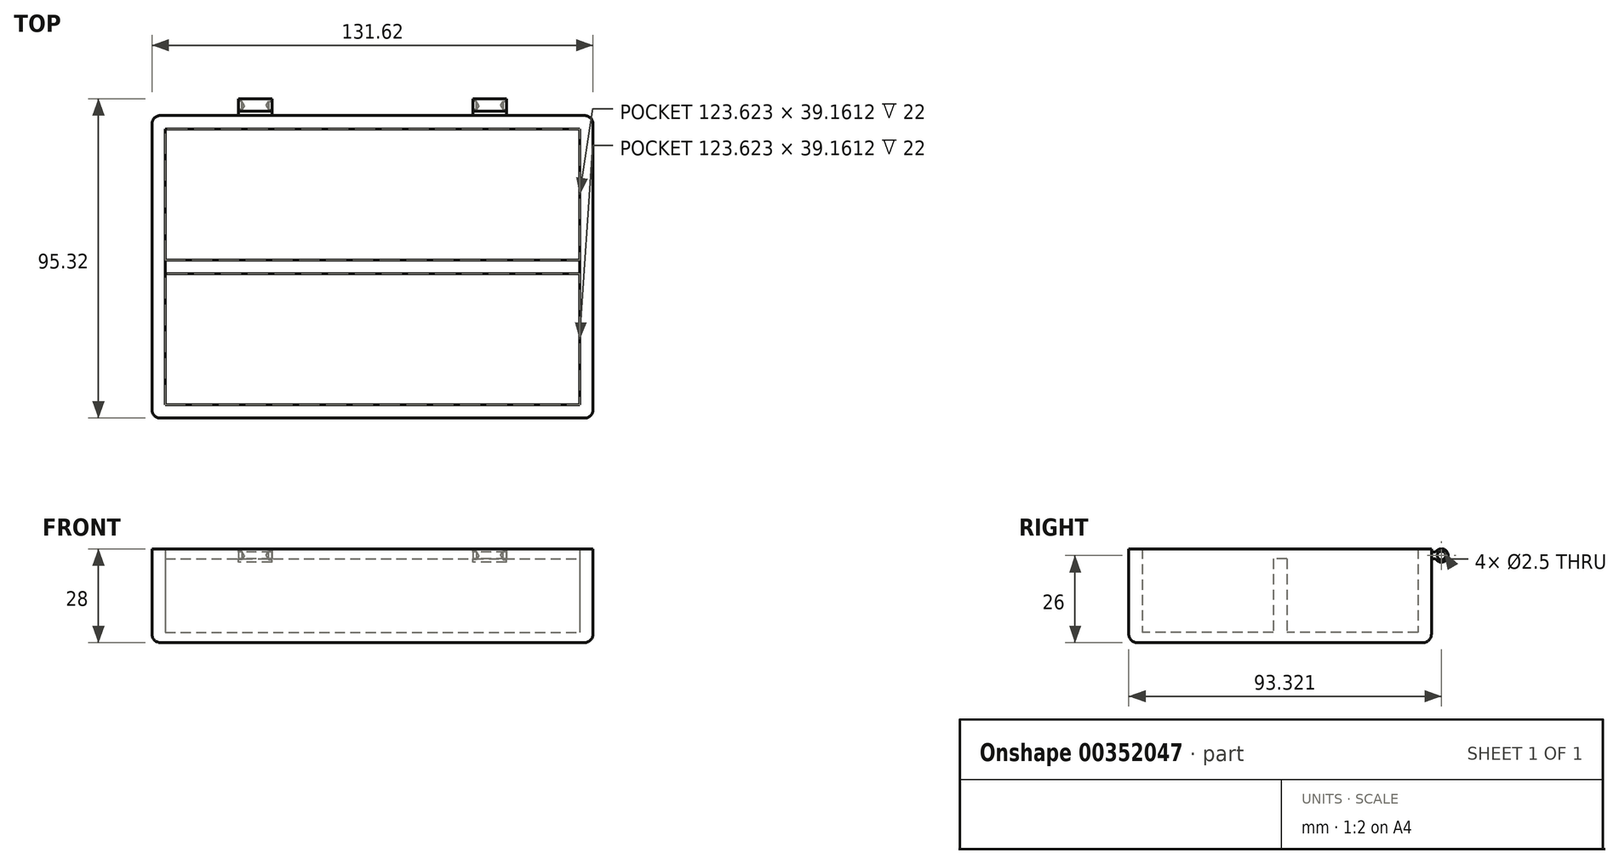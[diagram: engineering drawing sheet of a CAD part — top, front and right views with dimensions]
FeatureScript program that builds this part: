
annotation { "Feature Type Name" : "Feature", "Feature Type Description" : "" }
export const myFeature = defineFeature(function(context is Context, id is Id, definition is map)
    precondition{}
    {
        {
            var Q0;
            Q0=qCreatedBy(makeId("Top.planeOp"),FACE);
            var sketch = newSketch(context, id + "F0", { "sketchPlane" : qUnion([Q0])});
            skLineSegment(sketch, "E0.bottom", {"start": v(-65.81, 45.16) * mm, "end": v(65.81, 45.16) * mm});
            skLineSegment(sketch, "E0.top", {"start": v(-65.81, -45.16) * mm, "end": v(65.81, -45.16) * mm});
            skLineSegment(sketch, "E0.left", {"start": v(-65.81, 45.16) * mm, "end": v(-65.81, -45.16) * mm});
            skLineSegment(sketch, "E0.right", {"start": v(65.81, 45.16) * mm, "end": v(65.81, -45.16) * mm});
            skPoint(sketch, "E0.middle", {"position": v(0, 0) * mm});
            skSolve(sketch);
        }
        {
            var Q0;
            Q0 = qSketchRegion(id + "F0", true);
            extrude(context, id + "F1", {"entities" : qUnion([Q0]), "depth" : 3 * mm});
        }
        {
            var Q0;
            Q0=makeQuery(id+"F1.opExtrude","CAP_FACE",FACE,{"disambiguationData":[OSD([sQuery(id+"F0.wireOp",EDGE,"E0.bottom"),sQuery(id+"F0.wireOp",EDGE,"E0.top"),sQuery(id+"F0.wireOp",EDGE,"E0.left"),sQuery(id+"F0.wireOp",EDGE,"E0.right")])],"isStart":false});
            var sketch = newSketch(context, id + "F2", { "sketchPlane" : qUnion([Q0])});
            skLineSegment(sketch, "E1.bottom", {"start": v(-61.81, 41.16) * mm, "end": v(61.81, 41.16) * mm});
            skLineSegment(sketch, "E1.top", {"start": v(-61.81, -41.16) * mm, "end": v(61.81, -41.16) * mm});
            skLineSegment(sketch, "E1.left", {"start": v(-61.81, 41.16) * mm, "end": v(-61.81, -41.16) * mm});
            skLineSegment(sketch, "E1.right", {"start": v(61.81, 41.16) * mm, "end": v(61.81, -41.16) * mm});
            skPoint(sketch, "E1.middle", {"position": v(0, 0) * mm});
            skSolve(sketch);
        }
        {
            var Q0;
            Q0=makeQuery(id+"F2.imprint","IMPRINT",FACE,{"disambiguationData":[TD([[makeQuery(id+"F2.imprint","IMPRINT",EDGE,{"derivedFrom":sQuery(id+"F2.wireOp",EDGE,"E1.bottom")}),1.0]])]});
            extrude(context, id + "F3", {"entities" : qUnion([Q0]), "operationType" : NewBodyOperationType.ADD, "depth" : 25 * mm});
        }
        {
            var Q0;
            Q0=makeQuery(id+"F1.opExtrude","CAP_FACE",FACE,{"disambiguationData":[OSD([sQuery(id+"F0.wireOp",EDGE,"E0.bottom"),sQuery(id+"F0.wireOp",EDGE,"E0.top"),sQuery(id+"F0.wireOp",EDGE,"E0.left"),sQuery(id+"F0.wireOp",EDGE,"E0.right")])],"isStart":false});
            var sketch = newSketch(context, id + "F4", { "sketchPlane" : qUnion([Q0])});
            skLineSegment(sketch, "E2.bottom", {"start": v(-61.81, 41.16) * mm, "end": v(61.81, 41.16) * mm});
            skLineSegment(sketch, "E2.top", {"start": v(-61.81, 2) * mm, "end": v(61.81, 2) * mm});
            skLineSegment(sketch, "E2.left", {"start": v(-61.81, 41.16) * mm, "end": v(-61.81, 2) * mm});
            skLineSegment(sketch, "E2.right", {"start": v(61.81, 41.16) * mm, "end": v(61.81, 2) * mm});
            skLineSegment(sketch, "E3.bottom", {"start": v(-61.81, -2) * mm, "end": v(61.81, -2) * mm});
            skLineSegment(sketch, "E3.top", {"start": v(-61.81, -41.16) * mm, "end": v(61.81, -41.16) * mm});
            skLineSegment(sketch, "E3.left", {"start": v(-61.81, -2) * mm, "end": v(-61.81, -41.16) * mm});
            skLineSegment(sketch, "E3.right", {"start": v(61.81, -2) * mm, "end": v(61.81, -41.16) * mm});
            skSolve(sketch);
        }
        {
            var Q0;
            {var subQ0=sQuery(id+"F4.wireOp",EDGE,"E2.top");Q0=makeQuery(id+"F4.imprint","IMPRINT",FACE,{"disambiguationData":[TD([[makeQuery(id+"F4.imprint","IMPRINT",EDGE,{"derivedFrom":subQ0}),-1.0]])]});}
            extrude(context, id + "F5", {"entities" : qUnion([Q0]), "operationType" : NewBodyOperationType.ADD, "depth" : 25 * mm});
        }
        {
            var Q0;
            {var subQ0=sQuery(id+"F0.wireOp",EDGE,"E0.right");var subQ1=sQuery(id+"F0.wireOp",EDGE,"E0.bottom");Q0=makeQuery(id+"F3.boolean.opBoolean","MERGE",EDGE,{"derivedFrom":[makeQuery(id+"F1.opExtrude","SWEPT_EDGE",EDGE,{"disambiguationData":[OSD([subQ1,subQ0])]}),makeQuery(id+"F3.opExtrude","SWEPT_EDGE",EDGE,{"disambiguationData":[OSD([subQ1,subQ0])]})]});}
            var Q1;
            {var subQ0=sQuery(id+"F0.wireOp",EDGE,"E0.right");var subQ1=sQuery(id+"F0.wireOp",EDGE,"E0.top");Q1=makeQuery(id+"F3.boolean.opBoolean","MERGE",EDGE,{"derivedFrom":[makeQuery(id+"F1.opExtrude","SWEPT_EDGE",EDGE,{"disambiguationData":[OSD([subQ1,subQ0])]}),makeQuery(id+"F3.opExtrude","SWEPT_EDGE",EDGE,{"disambiguationData":[OSD([subQ1,subQ0])]})]});}
            var Q2;
            {var subQ0=sQuery(id+"F0.wireOp",EDGE,"E0.left");var subQ1=sQuery(id+"F0.wireOp",EDGE,"E0.top");Q2=makeQuery(id+"F3.boolean.opBoolean","MERGE",EDGE,{"derivedFrom":[makeQuery(id+"F1.opExtrude","SWEPT_EDGE",EDGE,{"disambiguationData":[OSD([subQ1,subQ0])]}),makeQuery(id+"F3.opExtrude","SWEPT_EDGE",EDGE,{"disambiguationData":[OSD([subQ1,subQ0])]})]});}
            var Q3;
            {var subQ0=sQuery(id+"F0.wireOp",EDGE,"E0.left");var subQ1=sQuery(id+"F0.wireOp",EDGE,"E0.bottom");Q3=makeQuery(id+"F3.boolean.opBoolean","MERGE",EDGE,{"derivedFrom":[makeQuery(id+"F1.opExtrude","SWEPT_EDGE",EDGE,{"disambiguationData":[OSD([subQ1,subQ0])]}),makeQuery(id+"F3.opExtrude","SWEPT_EDGE",EDGE,{"disambiguationData":[OSD([subQ1,subQ0])]})]});}
            var Q4;
            Q4=makeQuery(id+"F1.opExtrude","CAP_EDGE",EDGE,{"disambiguationData":[OSD([sQuery(id+"F0.wireOp",EDGE,"E0.bottom")])],"isStart":true});
            var Q5;
            Q5=makeQuery(id+"F1.opExtrude","CAP_EDGE",EDGE,{"disambiguationData":[OSD([sQuery(id+"F0.wireOp",EDGE,"E0.left")])],"isStart":true});
            var Q6;
            Q6=makeQuery(id+"F1.opExtrude","CAP_EDGE",EDGE,{"disambiguationData":[OSD([sQuery(id+"F0.wireOp",EDGE,"E0.top")])],"isStart":true});
            var Q7;
            Q7=makeQuery(id+"F1.opExtrude","CAP_EDGE",EDGE,{"disambiguationData":[OSD([sQuery(id+"F0.wireOp",EDGE,"E0.right")])],"isStart":true});
            fillet(context, id + "F6", {"entities" : qUnion([Q0, Q1, Q2, Q3, Q4, Q5, Q6, Q7]), "radius" : 2.5 * mm, "tangentPropagation" : true, "allowEdgeOverflow" : false});
        }
        {
            var Q0;
            {var subQ0=sQuery(id+"F0.wireOp",EDGE,"E0.bottom");Q0=makeQuery(id+"F3.boolean.opBoolean","MERGE",FACE,{"derivedFrom":[makeQuery(id+"F1.opExtrude","SWEPT_FACE",FACE,{"disambiguationData":[OSD([subQ0])]}),makeQuery(id+"F3.opExtrude","SWEPT_FACE",FACE,{"disambiguationData":[OSD([subQ0])]})]});}
            var sketch = newSketch(context, id + "F7", { "sketchPlane" : qUnion([Q0])});
            skLineSegment(sketch, "E4.bottom", {"start": v(-40, 28) * mm, "end": v(-30, 28) * mm});
            skLineSegment(sketch, "E4.top", {"start": v(-40, 24) * mm, "end": v(-30, 24) * mm});
            skLineSegment(sketch, "E4.left", {"start": v(-40, 28) * mm, "end": v(-40, 24) * mm});
            skLineSegment(sketch, "E4.right", {"start": v(-30, 28) * mm, "end": v(-30, 24) * mm});
            skLineSegment(sketch, "E5.MirrorCS", {"start": v(40, 24) * mm, "end": v(30, 24) * mm});
            skLineSegment(sketch, "E6.MirrorCS", {"start": v(40, 28) * mm, "end": v(30, 28) * mm});
            skLineSegment(sketch, "E7.MirrorCS", {"start": v(40, 28) * mm, "end": v(40, 24) * mm});
            skLineSegment(sketch, "E8.MirrorCS", {"start": v(30, 28) * mm, "end": v(30, 24) * mm});
            skSolve(sketch);
        }
        {
            var Q0;
            Q0 = qSketchRegion(id + "F7", true);
            extrude(context, id + "F8", {"entities" : qUnion([Q0]), "operationType" : NewBodyOperationType.ADD, "depth" : 5 * mm});
        }
        {
            var Q0;
            Q0=makeQuery(id+"F8.opExtrude","SWEPT_FACE",FACE,{"disambiguationData":[OSD([sQuery(id+"F7.wireOp",EDGE,"E4.right")])]});
            var sketch = newSketch(context, id + "F9", { "sketchPlane" : qUnion([Q0])});
            skLineSegment(sketch, "E9", {"start": v(-47.66, 28) * mm, "end": v(-47.66, 24) * mm, "construction": true});
            skLineSegment(sketch, "E10", {"start": v(-50.16, 26) * mm, "end": v(-45.16, 26) * mm, "construction": true});
            skCircle(sketch, "E11", {"center": v(-48.16, 26) * mm, "radius": 2 * mm});
            skLineSegment(sketch, "E12.bottom", {"start": v(-47.66, 25) * mm, "end": v(-45.16, 25) * mm});
            skLineSegment(sketch, "E12.top", {"start": v(-47.66, 27) * mm, "end": v(-45.16, 27) * mm});
            skLineSegment(sketch, "E12.left", {"start": v(-47.66, 25) * mm, "end": v(-47.66, 27) * mm});
            skLineSegment(sketch, "E12.right", {"start": v(-45.16, 25) * mm, "end": v(-45.16, 27) * mm});
            skSolve(sketch);
        }
        {
            var Q0;
            {var subQ0=sQuery(id+"F9.wireOp",EDGE,"E11");var subQ1=sQuery(id+"F7.wireOp",EDGE,"E4.right");var subQ4=makeQuery(id+"F8.opExtrude","CAP_EDGE",EDGE,{"disambiguationData":[OSD([subQ1])],"isStart":false});var subQ5=makeQuery(id+"F9.imprint","INTERSECT",VERTEX,{"derivedFrom":[subQ4,subQ0]});Q0=makeQuery(id+"F9.imprint","IMPRINT",FACE,{"disambiguationData":[TD([[makeQuery(id+"F9.imprint","IMPRINT",EDGE,{"disambiguationData":[TD([[subQ5,1.0]])],"derivedFrom":subQ0}),-1.0]])]});}
            var Q1;
            {var subQ0=sQuery(id+"F9.wireOp",EDGE,"E11");var subQ1=sQuery(id+"F7.wireOp",EDGE,"E4.right");var subQ2=makeQuery(id+"F8.opExtrude","CAP_EDGE",EDGE,{"disambiguationData":[OSD([subQ1])],"isStart":false});var subQ3=makeQuery(id+"F9.imprint","INTERSECT",VERTEX,{"derivedFrom":[subQ2,subQ0]});Q1=makeQuery(id+"F9.imprint","IMPRINT",FACE,{"disambiguationData":[TD([[makeQuery(id+"F9.imprint","IMPRINT",EDGE,{"disambiguationData":[TD([[subQ3,-1.0]])],"derivedFrom":subQ0}),-1.0]])]});}
            var Q2;
            {var subQ0=sQuery(id+"F9.wireOp",EDGE,"E12.bottom");var subQ1=sQuery(id+"F9.wireOp",EDGE,"E11");var subQ2=makeQuery(id+"F9.imprint","INTERSECT",VERTEX,{"derivedFrom":[subQ1,subQ0]});Q2=makeQuery(id+"F9.imprint","IMPRINT",FACE,{"disambiguationData":[TD([[makeQuery(id+"F9.imprint","IMPRINT",EDGE,{"disambiguationData":[TD([[subQ2,1.0]])],"derivedFrom":subQ1}),-1.0]])]});}
            var Q3;
            {var subQ0=sQuery(id+"F9.wireOp",EDGE,"E12.top");var subQ1=sQuery(id+"F9.wireOp",EDGE,"E11");var subQ2=makeQuery(id+"F9.imprint","INTERSECT",VERTEX,{"derivedFrom":[subQ1,subQ0]});Q3=makeQuery(id+"F9.imprint","IMPRINT",FACE,{"disambiguationData":[TD([[makeQuery(id+"F9.imprint","IMPRINT",EDGE,{"disambiguationData":[TD([[subQ2,-1.0]])],"derivedFrom":subQ0}),1.0]])]});}
            extrude(context, id + "F10", {"entities" : qUnion([Q0, Q1, Q2, Q3]), "operationType" : NewBodyOperationType.REMOVE, "oppositeDirection" : true, "depth" : 25 * mm, "hasSecondDirection" : true, "secondDirectionBound" : SecondDirectionBoundingType.THROUGH_ALL, "secondDirectionOppositeDirection" : false, "secondDirectionDepth" : 25 * mm});
        }
        {
            var Q0;
            Q0=makeQuery(id+"F8.opExtrude","SWEPT_FACE",FACE,{"disambiguationData":[OSD([sQuery(id+"F7.wireOp",EDGE,"E4.right")])]});
            var sketch = newSketch(context, id + "F11", { "sketchPlane" : qUnion([Q0])});
            skPoint(sketch, "E13", {"position": v(-48.16, 26) * mm});
            skSolve(sketch);
        }
        {
            var Q0;
            Q0=sQuery(id+"F11.wireOp",VERTEX,"E13");
            var Q1;
            Q1=makeQuery(id+"F1.opExtrude","SWEPT_BODY",BODY,{"disambiguationData":[OSD([sQuery(id+"F0.wireOp",EDGE,"E0.bottom"),sQuery(id+"F0.wireOp",EDGE,"E0.top"),sQuery(id+"F0.wireOp",EDGE,"E0.left"),sQuery(id+"F0.wireOp",EDGE,"E0.right")])]});
            hole(context, id + "F12", {"style" : HoleStyle.SIMPLE, "endStyle" : HoleEndStyle.BLIND, "holeDiameter" : 2.5 * mm, "holeDepth" : 1 * mm, "isTappedThrough" : true, "tappedDepth" : 12 * mm, "tapClearance" : 3, "locations" : qUnion([Q0]), "scope" : qUnion([Q1])});
        }
        {
            var Q0;
            Q0=makeQuery(id+"F8.opExtrude","SWEPT_FACE",FACE,{"disambiguationData":[OSD([sQuery(id+"F7.wireOp",EDGE,"E4.left")])]});
            var sketch = newSketch(context, id + "F13", { "sketchPlane" : qUnion([Q0])});
            skPoint(sketch, "E14", {"position": v(48.16, 26) * mm});
            skSolve(sketch);
        }
        {
            var Q0;
            Q0=sQuery(id+"F13.wireOp",VERTEX,"E14");
            var Q1;
            Q1=makeQuery(id+"F1.opExtrude","SWEPT_BODY",BODY,{"disambiguationData":[OSD([sQuery(id+"F0.wireOp",EDGE,"E0.bottom"),sQuery(id+"F0.wireOp",EDGE,"E0.top"),sQuery(id+"F0.wireOp",EDGE,"E0.left"),sQuery(id+"F0.wireOp",EDGE,"E0.right")])]});
            hole(context, id + "F14", {"style" : HoleStyle.SIMPLE, "endStyle" : HoleEndStyle.BLIND, "holeDiameter" : 2.5 * mm, "holeDepth" : 1 * mm, "isTappedThrough" : true, "tappedDepth" : 12 * mm, "tapClearance" : 3, "locations" : qUnion([Q0]), "scope" : qUnion([Q1])});
        }
        {
            var Q0;
            Q0=makeQuery(id+"F8.opExtrude","SWEPT_FACE",FACE,{"disambiguationData":[OSD([sQuery(id+"F7.wireOp",EDGE,"E8.MirrorCS")])]});
            var sketch = newSketch(context, id + "F15", { "sketchPlane" : qUnion([Q0])});
            skPoint(sketch, "E15", {"position": v(48.16, 26) * mm});
            skSolve(sketch);
        }
        {
            var Q0;
            Q0=sQuery(id+"F15.wireOp",VERTEX,"E15");
            var Q1;
            Q1=makeQuery(id+"F1.opExtrude","SWEPT_BODY",BODY,{"disambiguationData":[OSD([sQuery(id+"F0.wireOp",EDGE,"E0.bottom"),sQuery(id+"F0.wireOp",EDGE,"E0.top"),sQuery(id+"F0.wireOp",EDGE,"E0.left"),sQuery(id+"F0.wireOp",EDGE,"E0.right")])]});
            hole(context, id + "F16", {"style" : HoleStyle.SIMPLE, "endStyle" : HoleEndStyle.BLIND, "holeDiameter" : 2.5 * mm, "holeDepth" : 1 * mm, "isTappedThrough" : true, "tappedDepth" : 12 * mm, "tapClearance" : 3, "locations" : qUnion([Q0]), "scope" : qUnion([Q1])});
        }
        {
            var Q0;
            Q0=makeQuery(id+"F8.opExtrude","SWEPT_FACE",FACE,{"disambiguationData":[OSD([sQuery(id+"F7.wireOp",EDGE,"E7.MirrorCS")])]});
            var sketch = newSketch(context, id + "F17", { "sketchPlane" : qUnion([Q0])});
            skPoint(sketch, "E16", {"position": v(-48.16, 26) * mm});
            skSolve(sketch);
        }
        {
            var Q0;
            Q0=sQuery(id+"F17.wireOp",VERTEX,"E16");
            var Q1;
            Q1=makeQuery(id+"F1.opExtrude","SWEPT_BODY",BODY,{"disambiguationData":[OSD([sQuery(id+"F0.wireOp",EDGE,"E0.bottom"),sQuery(id+"F0.wireOp",EDGE,"E0.top"),sQuery(id+"F0.wireOp",EDGE,"E0.left"),sQuery(id+"F0.wireOp",EDGE,"E0.right")])]});
            hole(context, id + "F18", {"style" : HoleStyle.SIMPLE, "endStyle" : HoleEndStyle.BLIND, "holeDiameter" : 2.5 * mm, "holeDepth" : 1 * mm, "isTappedThrough" : true, "tappedDepth" : 12 * mm, "tapClearance" : 3, "locations" : qUnion([Q0]), "scope" : qUnion([Q1])});
        }
        {
            var Q0;
            {var subQ0=sQuery(id+"F2.wireOp",EDGE,"E1.right");var subQ1=sQuery(id+"F2.wireOp",EDGE,"E1.left");Q0=makeQuery(id+"F8.boolean.opBoolean","MERGE",FACE,{"derivedFrom":[makeQuery(id+"F5.boolean.opBoolean","MERGE",FACE,{"derivedFrom":[makeQuery(id+"F3.opExtrude","CAP_FACE",FACE,{"disambiguationData":[OSD([sQuery(id+"F0.wireOp",EDGE,"E0.bottom"),sQuery(id+"F0.wireOp",EDGE,"E0.top"),sQuery(id+"F0.wireOp",EDGE,"E0.left"),sQuery(id+"F0.wireOp",EDGE,"E0.right"),sQuery(id+"F2.wireOp",EDGE,"E1.bottom"),sQuery(id+"F2.wireOp",EDGE,"E1.top"),subQ1,subQ0])],"isStart":false}),makeQuery(id+"F5.opExtrude","CAP_FACE",FACE,{"disambiguationData":[OSD([subQ1,subQ0,sQuery(id+"F4.wireOp",EDGE,"E2.top"),sQuery(id+"F4.wireOp",EDGE,"E3.bottom")])],"isStart":false})]}),makeQuery(id+"F8.opExtrude","SWEPT_FACE",FACE,{"disambiguationData":[OSD([sQuery(id+"F7.wireOp",EDGE,"E4.bottom")])]}),makeQuery(id+"F8.opExtrude","SWEPT_FACE",FACE,{"disambiguationData":[OSD([sQuery(id+"F7.wireOp",EDGE,"E6.MirrorCS")])]})]});}
            var sketch = newSketch(context, id + "F19", { "sketchPlane" : qUnion([Q0])});
            skLineSegment(sketch, "E17.bottom", {"start": v(-61.81, 41.16) * mm, "end": v(61.81, 41.16) * mm});
            skLineSegment(sketch, "E17.top", {"start": v(-61.81, -41.16) * mm, "end": v(61.81, -41.16) * mm});
            skLineSegment(sketch, "E17.left", {"start": v(-61.81, 41.16) * mm, "end": v(-61.81, -41.16) * mm});
            skLineSegment(sketch, "E17.right", {"start": v(61.81, 41.16) * mm, "end": v(61.81, -41.16) * mm});
            skSolve(sketch);
        }
        {
            var Q0;
            Q0 = qSketchRegion(id + "F19", true);
            extrude(context, id + "F20", {"entities" : qUnion([Q0]), "operationType" : NewBodyOperationType.REMOVE, "oppositeDirection" : true, "depth" : 3 * mm});
        }
    });
